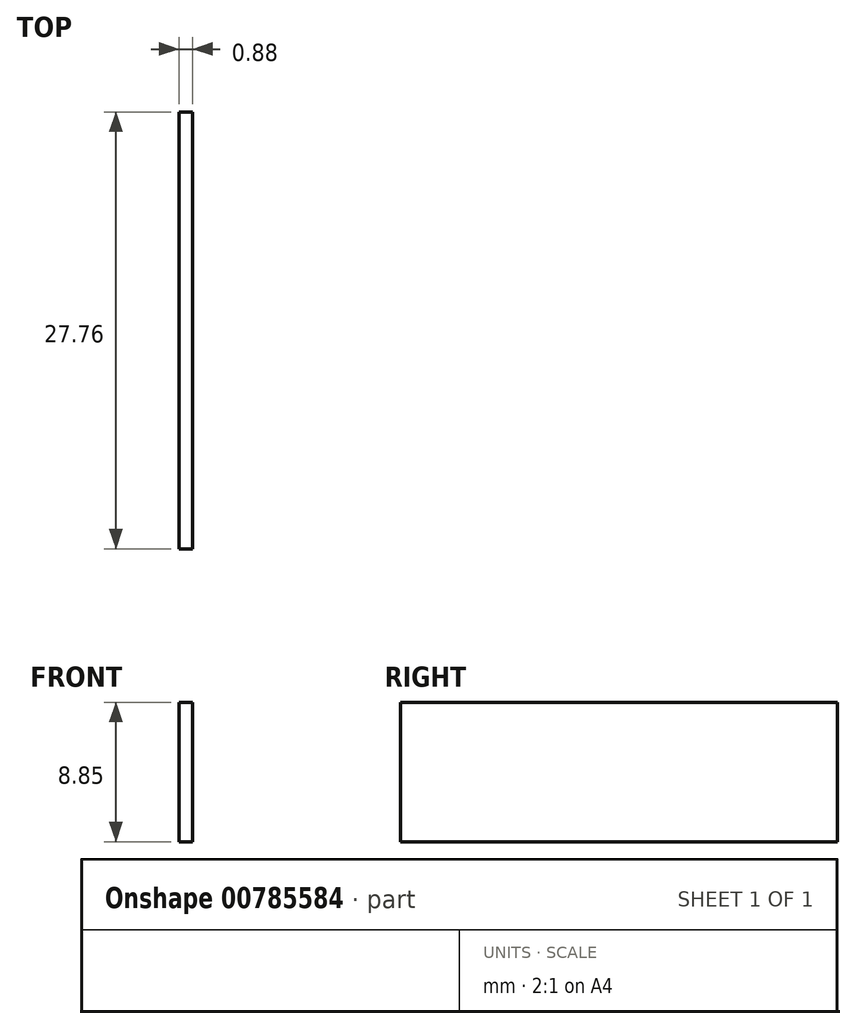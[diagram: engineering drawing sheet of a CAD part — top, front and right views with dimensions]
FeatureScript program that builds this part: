
annotation { "Feature Type Name" : "Feature", "Feature Type Description" : "" }
export const myFeature = defineFeature(function(context is Context, id is Id, definition is map)
    precondition{}
    {
        {
            var Q0;
            Q0=qCreatedBy(makeId("Front.planeOp"),FACE);
            var sketch = newSketch(context, id + "F0", { "sketchPlane" : qUnion([Q0])});
            skLineSegment(sketch, "E0.bottom", {"start": v(-48.5, 15.88) * mm, "end": v(-47.62, 15.88) * mm});
            skLineSegment(sketch, "E0.top", {"start": v(-48.5, 7.03) * mm, "end": v(-47.62, 7.03) * mm});
            skLineSegment(sketch, "E0.left", {"start": v(-48.5, 15.88) * mm, "end": v(-48.5, 7.03) * mm});
            skLineSegment(sketch, "E0.right", {"start": v(-47.62, 15.88) * mm, "end": v(-47.62, 7.03) * mm});
            skSolve(sketch);
        }
        {
            var Q0;
            Q0 = qSketchRegion(id + "F0", true);
            extrude(context, id + "F1", {"entities" : qUnion([Q0]), "oppositeDirection" : true, "depth" : 27.76 * mm, "offsetDistance" : 25.4 * mm});
        }
    });
